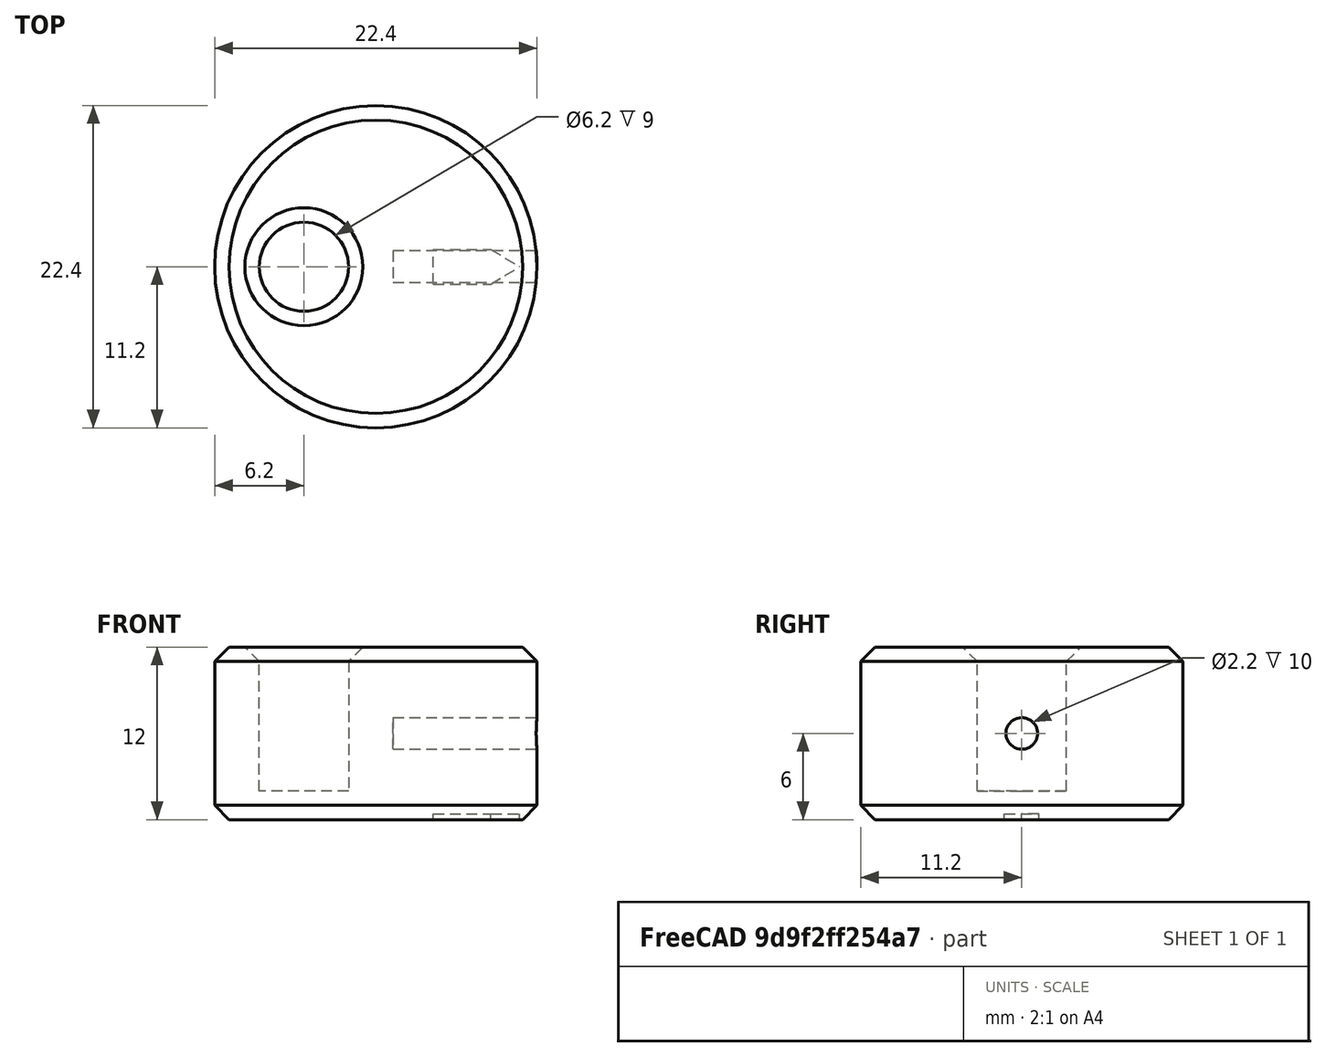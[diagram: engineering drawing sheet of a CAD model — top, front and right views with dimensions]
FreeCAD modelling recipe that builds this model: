
FCSTD DOCUMENT  (FreeCAD 0.21R33771 (Git))
Label: J-Pole_433_Top
Comment: J-Pole antenna top spacer for the radiator
License: CC BY-SA 4.0 (SPDX-ID: CC-BY-SA-4.0)
LicenseURL: https://creativecommons.org/licenses/by-sa/4.0/legalcode.txt
objects: Sketcher::SketchObject×4, PartDesign::Pocket×3, PartDesign::Chamfer×2, PartDesign::Pad×1, PartDesign::Body×1, Mesh::Feature×1
note: 17 computed .brp shape members not serialized (recipe doc carries the construction recipe); baked Part::Feature solids carry a one-line shape summary decoded from their .brp

FEATURE [Sketcher::SketchObject] Sketch
  FullyConstrained = true
  MapMode = 5
  Support = -> [XY_Plane]
  sketch-geometry (1):
    g0: Circle CenterX=0 CenterY=0 CenterZ=0 NormalX=0 NormalY=0 NormalZ=1 AngleXU=0 Radius=11.2
  constraints (2):
    c: Coincident(g0,g-1)
    c: Radius(g0) = 11.2
FEATURE [PartDesign::Pad] Pad
  Direction = (0,0,1)
  Length = 12
  Length2 = 10
  Profile = -> Sketch
  ReferenceAxis = -> Sketch [N_Axis]
  Type = 0
FEATURE [Sketcher::SketchObject] Sketch001
  FullyConstrained = true
  MapMode = 5
  Placement = pos=(0,0,12) rot=(0,0,1;0rad)
  Support = -> [Pad]
  sketch-geometry (1):
    g0: Circle CenterX=-5 CenterY=0 CenterZ=0 NormalX=0 NormalY=0 NormalZ=1 AngleXU=0 Radius=3.1
  constraints (3):
    c: PointOnObject(g0,g-1)
    c: Radius(g0) = 3.1
    c: Distance(g-1,g0) = 5
FEATURE [PartDesign::Pocket] Pocket
  BaseFeature = -> Pad
  Direction = (0,0,-1)
  Length = 10
  Length2 = 5
  Profile = -> Sketch001
  ReferenceAxis = -> Sketch001 [N_Axis]
  Type = 0
FEATURE [Sketcher::SketchObject] Sketch002
  ExternalGeometry = -> [Pocket]
  FullyConstrained = true
  MapMode = 5
  Placement = pos=(0,0,0) rot=(1,0,0;3.14159rad)
  Support = -> [Pocket]
  sketch-geometry (5):
    g0: LineSegment StartX=4 StartY=1.2 StartZ=0 EndX=4 EndY=-1.2 EndZ=0
    g1: LineSegment StartX=4 StartY=-1.2 StartZ=0 EndX=8 EndY=-1.2 EndZ=0
    g2: LineSegment StartX=4 StartY=1.2 StartZ=0 EndX=8 EndY=1.2 EndZ=0
    g3: LineSegment StartX=8 StartY=1.2 StartZ=0 EndX=10 EndY=0 EndZ=0
    g4: LineSegment StartX=8 StartY=-1.2 StartZ=0 EndX=10 EndY=0 EndZ=0
  constraints (15):
    c: Vertical(g0)
    c: Coincident(g1,g0)
    c: Horizontal(g1)
    c: Coincident(g2,g0)
    c: Horizontal(g2)
    c: Coincident(g4,g3)
    c: PointOnObject(g3,g-1)
    c: Distance(g3,g0) = 6
    c: DistanceX(g2,g2) = 4
    c: DistanceX(g1,g1) = 4
    c: Distance(g-3,g3) = 10
    c: Coincident(g1,g4)
    c: Coincident(g2,g3)
    c: DistanceY(g0,g0) = 2.4
    c: DistanceY(g-1,g0) = 1.2
FEATURE [PartDesign::Pocket] Pocket001
  BaseFeature = -> Pocket
  Direction = (0,0,1)
  Length = 0.4
  Length2 = 5
  Profile = -> Sketch002
  ReferenceAxis = -> Sketch002 [N_Axis]
  Type = 0
FEATURE [Sketcher::SketchObject] Sketch003
  AttachmentOffset = pos=(0,0,11.2) rot=(0,0,1;0rad)
  FullyConstrained = true
  MapMode = 5
  Placement = pos=(11.2,-2.5e-15,2.5e-15) rot=(0.57735,0.57735,0.57735;2.0944rad)
  Support = -> [YZ_Plane]
  sketch-geometry (1):
    g0: Circle CenterX=0 CenterY=6 CenterZ=0 NormalX=0 NormalY=0 NormalZ=1 AngleXU=0 Radius=1.1
  constraints (3):
    c: PointOnObject(g0,g-2)
    c: Radius(g0) = 1.1
    c: DistanceY(g-1,g0) = 6
FEATURE [PartDesign::Pocket] Pocket002
  BaseFeature = -> Pocket001
  Direction = (-1,2e-16,-3e-16)
  Length = 10
  Length2 = 5
  Profile = -> Sketch003
  ReferenceAxis = -> Sketch003 [N_Axis]
  Type = 0
FEATURE [PartDesign::Chamfer] Chamfer
  Angle = 45
  Base = -> Pocket002 [Edge1,Edge5]
  BaseFeature = -> Pocket002
  ChamferType = 0
  FlipDirection = false
  Size = 1
  Size2 = 1
  SupportTransform = false
  UseAllEdges = false
FEATURE [PartDesign::Chamfer] Chamfer001
  Angle = 45
  Base = -> Chamfer [Edge19]
  BaseFeature = -> Chamfer
  ChamferType = 0
  FlipDirection = false
  Size = 1
  Size2 = 1
  SupportTransform = false
  UseAllEdges = false
FEATURE [PartDesign::Body] Body
  Group = -> [Sketch,Pad,Sketch001,Pocket,Sketch002,Pocket001,Sketch003,Pocket002,Chamfer,Chamfer001]
  Origin = -> Origin
  Tip = -> Chamfer001
FEATURE [Mesh::Feature] Mesh  label="J-Pole_433_Top"
